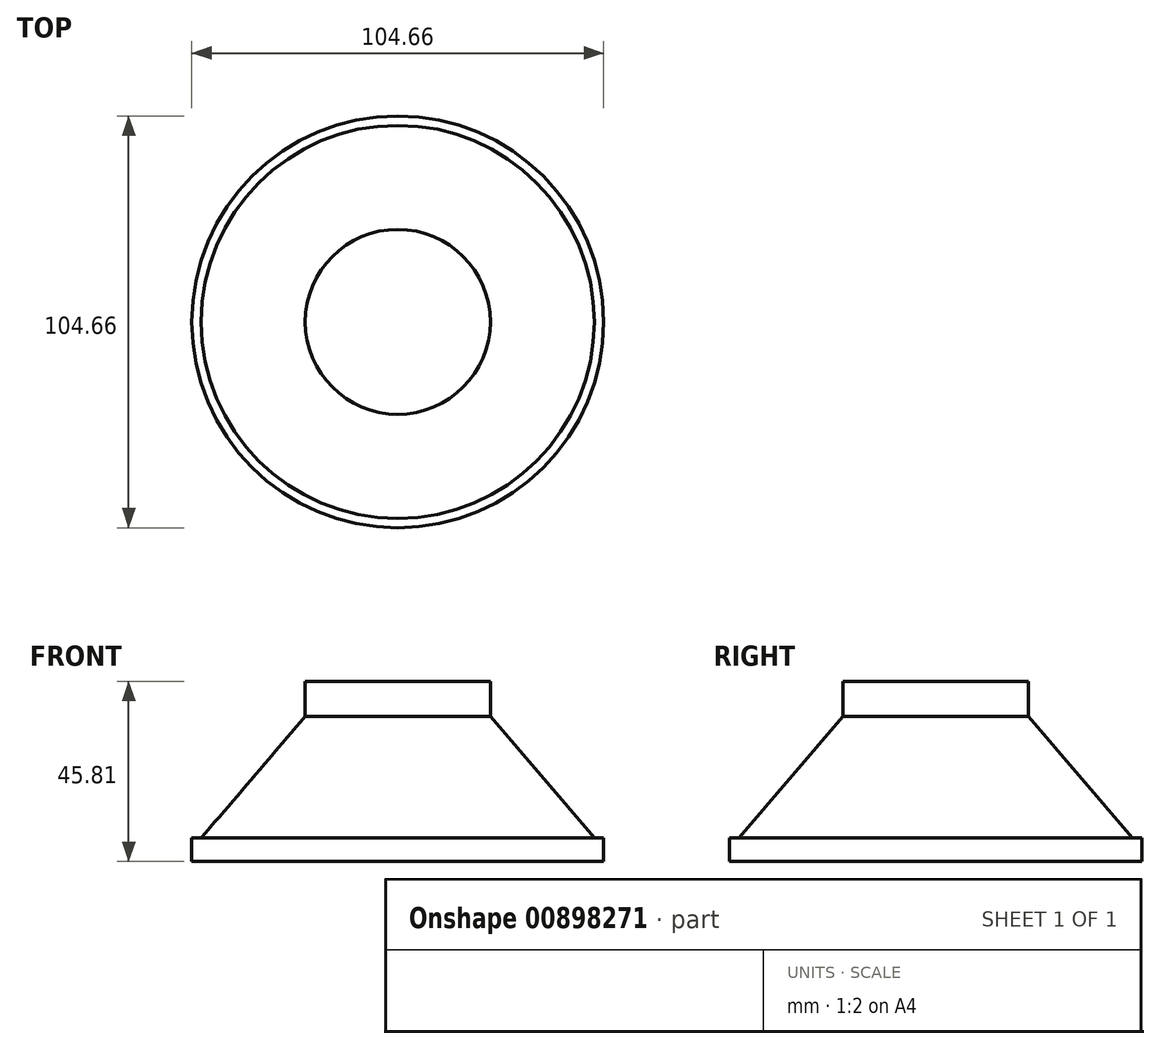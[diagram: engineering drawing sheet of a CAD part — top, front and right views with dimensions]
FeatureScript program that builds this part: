
annotation { "Feature Type Name" : "Feature", "Feature Type Description" : "" }
export const myFeature = defineFeature(function(context is Context, id is Id, definition is map)
    precondition{}
    {
        {
            var Q0;
            Q0=qCreatedBy(makeId("Front.planeOp"),FACE);
            var sketch = newSketch(context, id + "F0", { "sketchPlane" : qUnion([Q0])});
            skLineSegment(sketch, "E0", {"start": v(0, 45.8) * mm, "end": v(23.5, 45.8) * mm});
            skLineSegment(sketch, "E1", {"start": v(23.5, 45.8) * mm, "end": v(23.5, 36.89) * mm});
            skLineSegment(sketch, "E2", {"start": v(23.5, 36.89) * mm, "end": v(49.92, 6) * mm});
            skLineSegment(sketch, "E3", {"start": v(49.92, 6) * mm, "end": v(52.33, 6) * mm});
            skLineSegment(sketch, "E4", {"start": v(52.33, 6) * mm, "end": v(52.33, 0) * mm});
            skLineSegment(sketch, "E5", {"start": v(52.33, 0) * mm, "end": v(0, 0) * mm});
            skLineSegment(sketch, "E6", {"start": v(0, 0) * mm, "end": v(0, 45.8) * mm});
            skSolve(sketch);
        }
        {
            var Q0;
            Q0=makeQuery(id+"F0.imprint","IMPRINT",FACE,{"disambiguationData":[TD([[makeQuery(id+"F0.imprint","IMPRINT",EDGE,{"derivedFrom":sQuery(id+"F0.wireOp",EDGE,"E0")}),-1.0]])]});
            var Q1;
            Q1=sQuery(id+"F0.wireOp",EDGE,"E1");
            var Q2;
            Q2=sQuery(id+"F0.wireOp",EDGE,"E2");
            var Q3;
            Q3=sQuery(id+"F0.wireOp",EDGE,"E4");
            var Q4;
            Q4=sQuery(id+"F0.wireOp",EDGE,"E6");
            revolve(context, id + "F1", {"surfaceOperationType" : NewSurfaceOperationType.NEW, "entities" : qUnion([Q0]), "surfaceEntities" : qUnion([Q1, Q2, Q3]), "axis" : qUnion([Q4]), "revolveType" : RevolveType.FULL});
        }
    });
